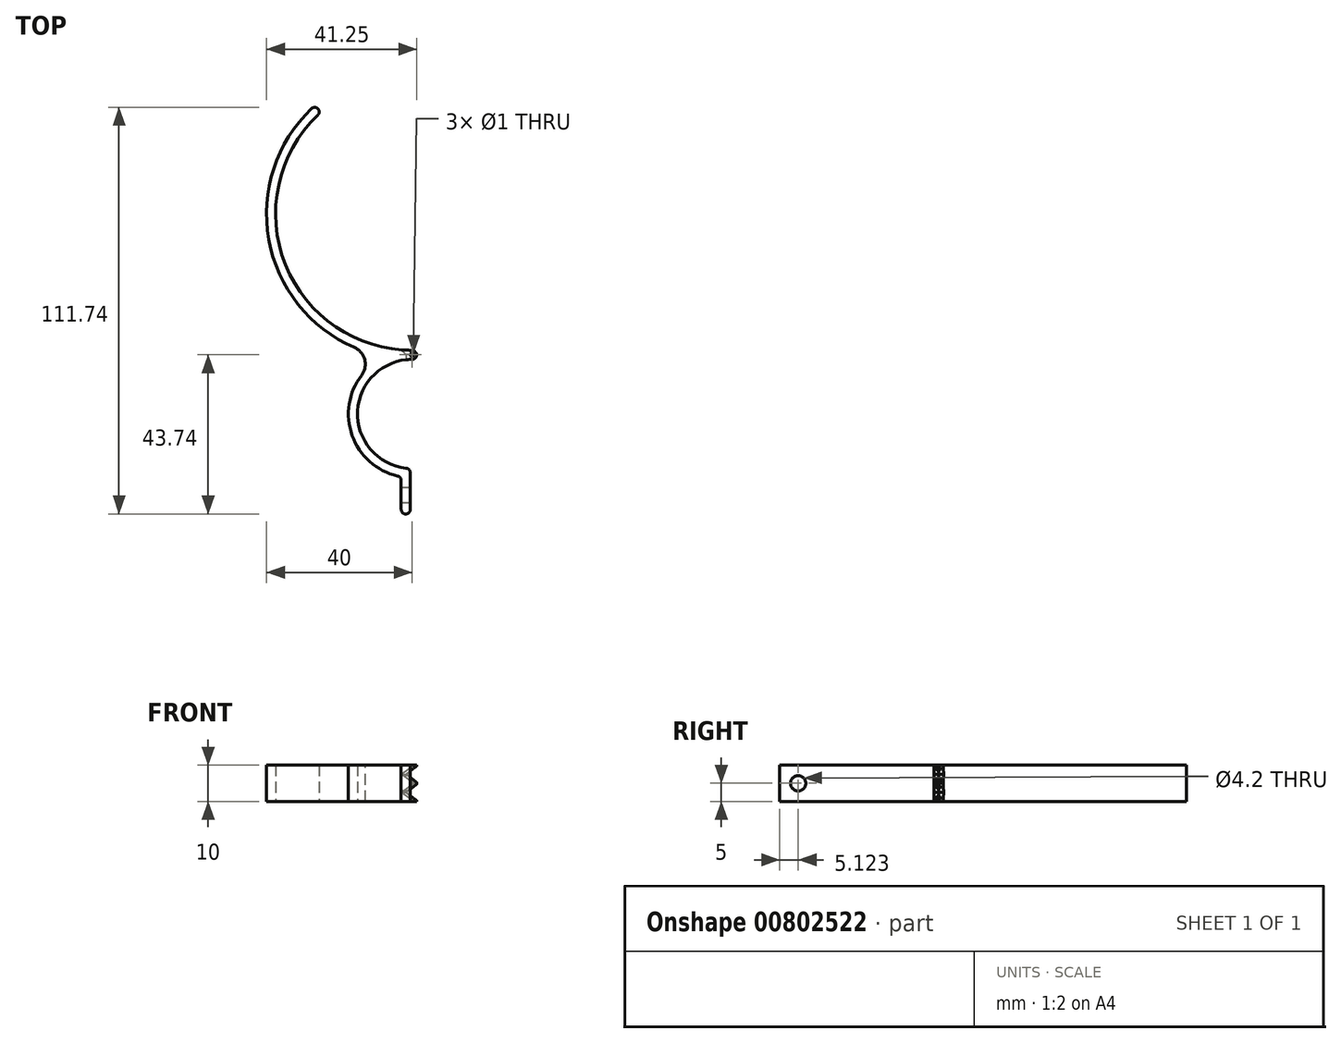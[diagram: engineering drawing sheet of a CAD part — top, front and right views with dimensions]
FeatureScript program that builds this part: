
annotation { "Feature Type Name" : "Feature", "Feature Type Description" : "" }
export const myFeature = defineFeature(function(context is Context, id is Id, definition is map)
    precondition{}
    {
        {
            var Q0;
            Q0=qCreatedBy(makeId("Top.planeOp"),FACE);
            var sketch = newSketch(context, id + "F0", { "sketchPlane" : qUnion([Q0])});
            skCircle(sketch, "E0", {"center": v(0, 0) * mm, "radius": 1.25 * mm});
            skArc(sketch, "E1", {"start": v(0, -1.25) * mm, "mid": v(-15, -16) * mm, "end": v(-0.5, -31.24) * mm});
            skArc(sketch, "E2.0", {"start": v(0, 1.25) * mm, "mid": v(-17.5, -16) * mm, "end": v(-0.5, -33.74) * mm});
            skArc(sketch, "E3", {"start": v(0, 76.25) * mm, "mid": v(-37.5, 38.75) * mm, "end": v(0, 1.25) * mm});
            skArc(sketch, "E4.0", {"start": v(0, 78.75) * mm, "mid": v(-40, 38.75) * mm, "end": v(0, -1.25) * mm});
            skLineSegment(sketch, "E5", {"start": v(0, 78.75) * mm, "end": v(0, 76.25) * mm});
            skLineSegment(sketch, "E6.bottom", {"start": v(-0.5, -31.24) * mm, "end": v(-3, -31.24) * mm});
            skLineSegment(sketch, "E6.top", {"start": v(-0.5, -43.74) * mm, "end": v(-3, -43.74) * mm});
            skLineSegment(sketch, "E6.left", {"start": v(-0.5, -31.24) * mm, "end": v(-0.5, -43.74) * mm});
            skLineSegment(sketch, "E6.right", {"start": v(-3, -31.24) * mm, "end": v(-3, -43.74) * mm});
            skPoint(sketch, "E7", {"position": v(-0.5, -33.74) * mm});
            skPoint(sketch, "E8.orphan", {"position": v(0, -31.25) * mm});
            skSolve(sketch);
        }
        {
            var Q0;
            Q0 = qSketchRegion(id + "F0", true);
            extrude(context, id + "F1", {"entities" : qUnion([Q0]), "depth" : 10 * mm, "offsetDistance" : 25 * mm});
        }
        {
            var Q0;
            Q0=qCreatedBy(makeId("Top.planeOp"),FACE);
            var sketch = newSketch(context, id + "F2", { "sketchPlane" : qUnion([Q0])});
            skLineSegment(sketch, "E9.bottom", {"start": v(-22.5, 68.75) * mm, "end": v(22.5, 68.75) * mm, "construction": true});
            skLineSegment(sketch, "E9.top", {"start": v(-22.5, 8.75) * mm, "end": v(22.5, 8.75) * mm, "construction": true});
            skLineSegment(sketch, "E9.left", {"start": v(-22.5, 68.75) * mm, "end": v(-22.5, 8.75) * mm, "construction": true});
            skLineSegment(sketch, "E9.right", {"start": v(22.5, 68.75) * mm, "end": v(22.5, 8.75) * mm, "construction": true});
            skPoint(sketch, "E10", {"position": v(0, 68.75) * mm});
            skLineSegment(sketch, "E11.bottom", {"start": v(-22.5, 68.75) * mm, "end": v(22.5, 68.75) * mm});
            skLineSegment(sketch, "E11.top", {"start": v(-22.5, 78.75) * mm, "end": v(22.5, 78.75) * mm});
            skLineSegment(sketch, "E11.left", {"start": v(-22.5, 68.75) * mm, "end": v(-22.5, 78.75) * mm});
            skLineSegment(sketch, "E11.right", {"start": v(22.5, 68.75) * mm, "end": v(22.5, 78.75) * mm});
            skSolve(sketch);
        }
        {
            var Q0;
            Q0=makeQuery(id+"F2.imprint","IMPRINT",FACE,{"disambiguationData":[TD([[makeQuery(id+"F2.imprint","IMPRINT",EDGE,{"derivedFrom":sQuery(id+"F2.wireOp",EDGE,"E11.bottom")}),1.0]])]});
            var Q1;
            Q1=makeQuery(id+"F1.opExtrude","CAP_FACE",FACE,{"disambiguationData":[OSD([sQuery(id+"F0.wireOp",EDGE,"E0"),sQuery(id+"F0.wireOp",EDGE,"E1"),sQuery(id+"F0.wireOp",EDGE,"E2.0"),sQuery(id+"F0.wireOp",EDGE,"E3"),sQuery(id+"F0.wireOp",EDGE,"E4.0"),sQuery(id+"F0.wireOp",EDGE,"E5"),sQuery(id+"F0.wireOp",EDGE,"E6.top"),sQuery(id+"F0.wireOp",EDGE,"E6.left"),sQuery(id+"F0.wireOp",EDGE,"E6.right")])],"isStart":false});
            extrude(context, id + "F3", {"entities" : qUnion([Q0]), "operationType" : NewBodyOperationType.REMOVE, "endBound" : BoundingType.UP_TO_SURFACE, "depth" : 25 * mm, "endBoundEntityFace" : qUnion([Q1]), "offsetDistance" : 25 * mm});
        }
        {
            var Q0;
            Q0=makeQuery(id+"F1.opExtrude","CAP_FACE",FACE,{"disambiguationData":[OSD([sQuery(id+"F0.wireOp",EDGE,"E0"),sQuery(id+"F0.wireOp",EDGE,"E1"),sQuery(id+"F0.wireOp",EDGE,"E2.0"),sQuery(id+"F0.wireOp",EDGE,"E3"),sQuery(id+"F0.wireOp",EDGE,"E4.0"),sQuery(id+"F0.wireOp",EDGE,"E5"),sQuery(id+"F0.wireOp",EDGE,"E6.top"),sQuery(id+"F0.wireOp",EDGE,"E6.left"),sQuery(id+"F0.wireOp",EDGE,"E6.right")])],"isStart":false});
            var sketch = newSketch(context, id + "F4", { "sketchPlane" : qUnion([Q0])});
            skCircle(sketch, "E12", {"center": v(0, 0) * mm, "radius": 0.5 * mm});
            skSolve(sketch);
        }
        {
            var Q0;
            Q0=makeQuery(id+"F4.imprint","IMPRINT",FACE,{"disambiguationData":[TD([[makeQuery(id+"F4.imprint","IMPRINT",EDGE,{"derivedFrom":sQuery(id+"F4.wireOp",EDGE,"E12")}),1.0]])]});
            var Q1;
            Q1=sQuery(id+"F4.wireOp",EDGE,"E12");
            extrude(context, id + "F5", {"entities" : qUnion([Q0]), "operationType" : NewBodyOperationType.REMOVE, "surfaceEntities" : qUnion([Q1]), "endBound" : BoundingType.UP_TO_NEXT, "oppositeDirection" : true, "depth" : 25 * mm, "offsetDistance" : 25 * mm});
        }
        {
            var Q0;
            Q0=makeQuery(id+"F1.opExtrude","SWEPT_FACE",FACE,{"disambiguationData":[OSD([sQuery(id+"F0.wireOp",EDGE,"E6.right")])]});
            var sketch = newSketch(context, id + "F6", { "sketchPlane" : qUnion([Q0])});
            skCircle(sketch, "E13", {"center": v(38.62, 5) * mm, "radius": 2.1 * mm});
            skSolve(sketch);
        }
        {
            var Q0;
            Q0=makeQuery(id+"F6.imprint","IMPRINT",FACE,{"disambiguationData":[TD([[makeQuery(id+"F6.imprint","IMPRINT",EDGE,{"derivedFrom":sQuery(id+"F6.wireOp",EDGE,"E13")}),1.0]])]});
            extrude(context, id + "F7", {"entities" : qUnion([Q0]), "operationType" : NewBodyOperationType.REMOVE, "endBound" : BoundingType.UP_TO_NEXT, "oppositeDirection" : true, "depth" : 25 * mm, "offsetDistance" : 25 * mm});
        }
        {
            var Q0;
            Q0=makeQuery(id+"F3.boolean.opBoolean","INTERSECT",EDGE,{"derivedFrom":[makeQuery(id+"F1.opExtrude","SWEPT_FACE",FACE,{"disambiguationData":[OSD([sQuery(id+"F0.wireOp",EDGE,"E4.0")])]}),makeQuery(id+"F3.opExtrude","SWEPT_FACE",FACE,{"disambiguationData":[OSD([sQuery(id+"F2.wireOp",EDGE,"E11.left")])]})]});
            var Q1;
            Q1=makeQuery(id+"F1.opExtrude","SWEPT_EDGE",EDGE,{"disambiguationData":[OSD([sQuery(id+"F0.wireOp",EDGE,"E2.0"),sQuery(id+"F0.wireOp",EDGE,"E4.0")])]});
            fillet(context, id + "F8", {"entities" : qUnion([Q0, Q1]), "radius" : 5 * mm, "tangentPropagation" : true, "allowEdgeOverflow" : false});
        }
        {
            var Q0;
            Q0=makeQuery(id+"F1.opExtrude","SWEPT_EDGE",EDGE,{"disambiguationData":[OSD([sQuery(id+"F0.wireOp",EDGE,"E2.0"),sQuery(id+"F0.wireOp",EDGE,"E6.right")])]});
            var Q1;
            Q1=makeQuery(id+"F1.opExtrude","SWEPT_EDGE",EDGE,{"disambiguationData":[OSD([sQuery(id+"F0.wireOp",EDGE,"E1"),sQuery(id+"F0.wireOp",EDGE,"E6.bottom"),sQuery(id+"F0.wireOp",EDGE,"E6.left")])]});
            var Q2;
            Q2=makeQuery(id+"F1.opExtrude","SWEPT_EDGE",EDGE,{"disambiguationData":[OSD([sQuery(id+"F0.wireOp",EDGE,"E6.top"),sQuery(id+"F0.wireOp",EDGE,"E6.left")])]});
            var Q3;
            Q3=makeQuery(id+"F1.opExtrude","SWEPT_EDGE",EDGE,{"disambiguationData":[OSD([sQuery(id+"F0.wireOp",EDGE,"E6.top"),sQuery(id+"F0.wireOp",EDGE,"E6.right")])]});
            var Q4;
            Q4=makeQuery(id+"F8.opFillet","BLEND_EDGE",EDGE,{"blendedFrom":[makeQuery(id+"F3.boolean.opBoolean","INTERSECT",EDGE,{"derivedFrom":[makeQuery(id+"F1.opExtrude","SWEPT_FACE",FACE,{"disambiguationData":[OSD([sQuery(id+"F0.wireOp",EDGE,"E4.0")])]}),makeQuery(id+"F3.opExtrude","SWEPT_FACE",FACE,{"disambiguationData":[OSD([sQuery(id+"F2.wireOp",EDGE,"E11.left")])]})]}),makeQuery(id+"F1.opExtrude","SWEPT_FACE",FACE,{"disambiguationData":[OSD([sQuery(id+"F0.wireOp",EDGE,"E3")])]})],"blendedInto":[makeQuery(id+"F1.opExtrude","SWEPT_FACE",FACE,{"disambiguationData":[OSD([sQuery(id+"F0.wireOp",EDGE,"E3")])]})]});
            fillet(context, id + "F9", {"entities" : qUnion([Q0, Q1, Q2, Q3, Q4]), "radius" : 1.25 * mm, "tangentPropagation" : true, "allowEdgeOverflow" : false});
        }
        {
            var Q0;
            Q0=qCreatedBy(makeId("Front.planeOp"),FACE);
            var sketch = newSketch(context, id + "F10", { "sketchPlane" : qUnion([Q0])});
            skLineSegment(sketch, "E14", {"start": v(1.25, 4.42) * mm, "end": v(-1.25, 2.5) * mm, "construction": true});
            skLineSegment(sketch, "E15", {"start": v(-1.25, 2.5) * mm, "end": v(1.25, 0.58) * mm, "construction": true});
            skLineSegment(sketch, "E16.0.0", {"start": v(0, 0) * mm, "end": v(1.25, 0) * mm, "construction": true});
            skLineSegment(sketch, "E16.0.1", {"start": v(0, 0) * mm, "end": v(0, 10) * mm, "construction": true});
            skLineSegment(sketch, "E16.0.2", {"start": v(0, 10) * mm, "end": v(1.25, 10) * mm, "construction": true});
            skLineSegment(sketch, "E16.0.3", {"start": v(0, 10) * mm, "end": v(0, 0) * mm, "construction": true});
            skLineSegment(sketch, "E17", {"start": v(-1.25, 2.5) * mm, "end": v(1.25, 2.5) * mm, "construction": true});
            skPoint(sketch, "E18", {"position": v(0, 2.5) * mm});
            skLineSegment(sketch, "E19", {"start": v(1.25, 4.42) * mm, "end": v(1.25, 0.58) * mm, "construction": true});
            skLineSegment(sketch, "E20", {"start": v(0, 5) * mm, "end": v(1.25, 5) * mm, "construction": true});
            skLineSegment(sketch, "E21.0", {"start": v(1.5, 4.93) * mm, "end": v(-1.66, 2.5) * mm});
            skLineSegment(sketch, "E21.1", {"start": v(1.5, 4.93) * mm, "end": v(1.5, 0.07) * mm});
            skLineSegment(sketch, "E21.2", {"start": v(-1.66, 2.5) * mm, "end": v(1.5, 0.07) * mm});
            skLineSegment(sketch, "E22.MirrorCS", {"start": v(-1.66, 7.5) * mm, "end": v(1.5, 9.93) * mm});
            skLineSegment(sketch, "E23.MirrorCS", {"start": v(1.5, 5.07) * mm, "end": v(-1.66, 7.5) * mm});
            skLineSegment(sketch, "E24.MirrorCS", {"start": v(1.5, 5.07) * mm, "end": v(1.5, 9.93) * mm});
            skSolve(sketch);
        }
        {
            var Q0;
            Q0 = qSketchRegion(id + "F10", true);
            extrude(context, id + "F11", {"entities" : qUnion([Q0]), "operationType" : NewBodyOperationType.REMOVE, "oppositeDirection" : true, "depth" : 5 * mm, "offsetDistance" : 25 * mm, "hasDraft" : true, "draftAngle" : 30 * degree, "hasSecondDirection" : true, "secondDirectionOppositeDirection" : false, "secondDirectionDepth" : 5 * mm});
        }
    });
